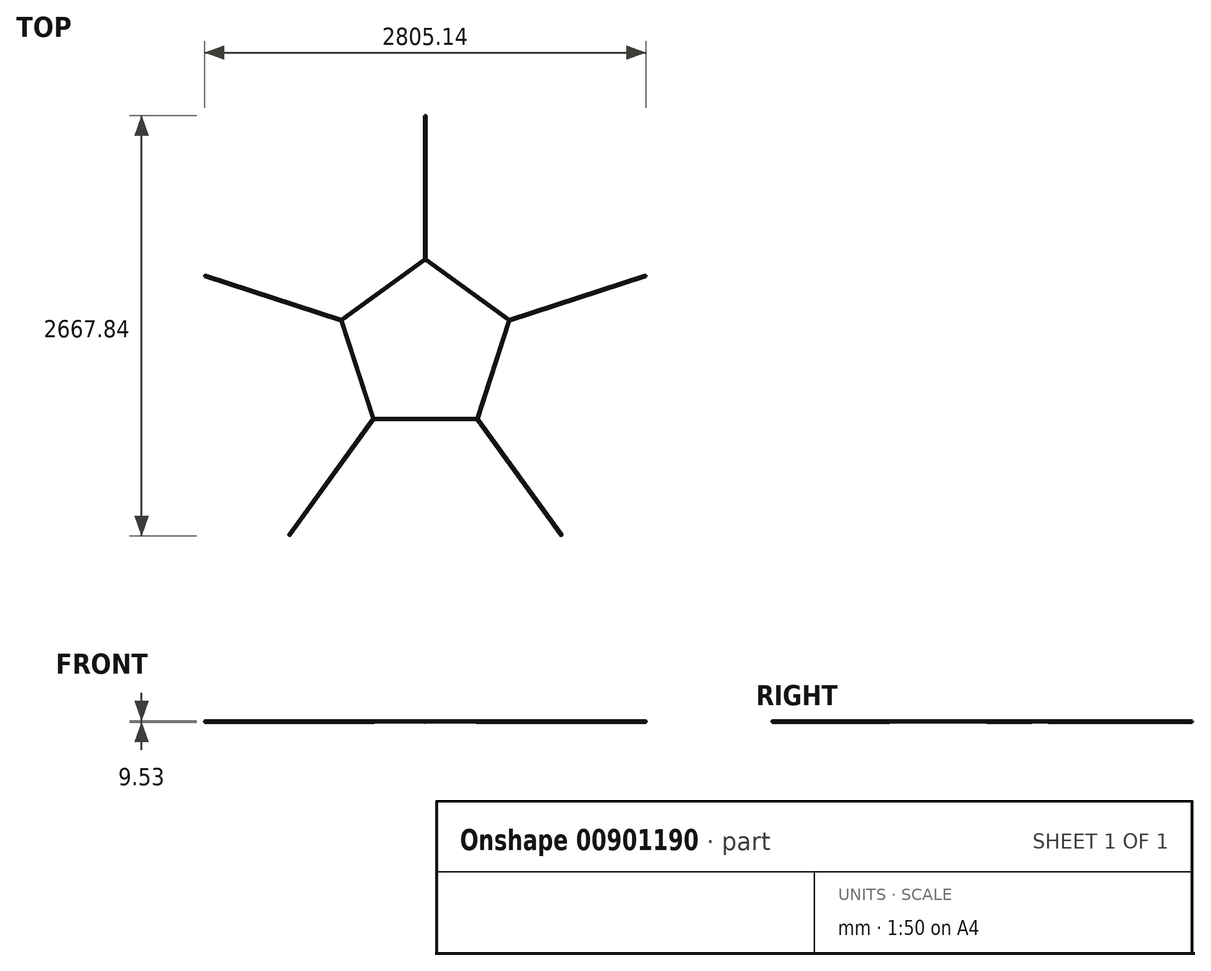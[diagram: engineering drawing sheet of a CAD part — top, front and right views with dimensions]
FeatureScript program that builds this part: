
annotation { "Feature Type Name" : "Feature", "Feature Type Description" : "" }
export const myFeature = defineFeature(function(context is Context, id is Id, definition is map)
    precondition{}
    {
        {
            var Q0;
            Q0=qCreatedBy(makeId("Top.planeOp"),FACE);
            var sketch = newSketch(context, id + "F0", { "sketchPlane" : qUnion([Q0])});
            skCircle(sketch, "E0.cCircle", {"center": v(0, 0) * mm, "radius": 450.85 * mm, "construction": true});
            skLineSegment(sketch, "E0.0", {"start": v(0, 557.28) * mm, "end": v(530, 172.2) * mm});
            skLineSegment(sketch, "E0.1", {"start": v(530, 172.2) * mm, "end": v(327.56, -450.85) * mm});
            skLineSegment(sketch, "E0.2", {"start": v(327.56, -450.85) * mm, "end": v(-327.56, -450.85) * mm});
            skLineSegment(sketch, "E0.3", {"start": v(-327.56, -450.85) * mm, "end": v(-530, 172.2) * mm});
            skLineSegment(sketch, "E0.4", {"start": v(-530, 172.2) * mm, "end": v(0, 557.28) * mm});
            skPoint(sketch, "E0.0.midPoint", {"position": v(265, 364.75) * mm});
            skCircle(sketch, "E1.cCircle", {"center": v(0, 0) * mm, "radius": 457.2 * mm, "construction": true});
            skLineSegment(sketch, "E1.0", {"start": v(0, 565.13) * mm, "end": v(537.47, 174.63) * mm});
            skLineSegment(sketch, "E1.1", {"start": v(537.47, 174.63) * mm, "end": v(332.18, -457.2) * mm});
            skLineSegment(sketch, "E1.2", {"start": v(332.18, -457.2) * mm, "end": v(-332.18, -457.2) * mm});
            skLineSegment(sketch, "E1.3", {"start": v(-332.18, -457.2) * mm, "end": v(-537.47, 174.63) * mm});
            skLineSegment(sketch, "E1.4", {"start": v(-537.47, 174.63) * mm, "end": v(0, 565.13) * mm});
            skPoint(sketch, "E1.0.midPoint", {"position": v(268.74, 369.88) * mm});
            skLineSegment(sketch, "E2", {"start": v(0, 0) * mm, "end": v(0, 903.65) * mm, "construction": true});
            skSolve(sketch);
        }
        {
            var Q0;
            Q0=makeQuery(id+"F0.imprint","IMPRINT",FACE,{"disambiguationData":[TD([[makeQuery(id+"F0.imprint","IMPRINT",EDGE,{"derivedFrom":sQuery(id+"F0.wireOp",EDGE,"E0.0")}),1.0]])]});
            extrude(context, id + "F1", {"entities" : qUnion([Q0]), "depth" : 6.35 * mm, "offsetDistance" : 25.4 * mm});
        }
        {
            var Q0;
            Q0=qCreatedBy(makeId("Front.planeOp"),FACE);
            var sketch = newSketch(context, id + "F2", { "sketchPlane" : qUnion([Q0])});
            skCircle(sketch, "E3", {"center": v(0, 3.18) * mm, "radius": 4.76 * mm});
            skSolve(sketch);
        }
        {
            var Q0;
            Q0=qCreatedBy(makeId("Front.planeOp"),FACE);
            var sketch = newSketch(context, id + "F3", { "sketchPlane" : qUnion([Q0])});
            skLineSegment(sketch, "E4", {"start": v(0, 0) * mm, "end": v(0, 50.6) * mm});
            skSolve(sketch);
        }
        {
            var Q0;
            Q0=makeQuery(id+"F2.imprint","IMPRINT",FACE,{"disambiguationData":[TD([[makeQuery(id+"F2.imprint","IMPRINT",EDGE,{"derivedFrom":sQuery(id+"F2.wireOp",EDGE,"E3")}),1.0]])]});
            extrude(context, id + "F4", {"entities" : qUnion([Q0]), "operationType" : NewBodyOperationType.ADD, "oppositeDirection" : true, "depth" : 1473.2 * mm, "offsetDistance" : 25.4 * mm});
        }
        {
            var Q0;
            Q0=makeQuery(id+"F1.opExtrude","SWEPT_BODY",BODY,{"disambiguationData":[OSD([sQuery(id+"F0.wireOp",EDGE,"E0.0"),sQuery(id+"F0.wireOp",EDGE,"E0.1"),sQuery(id+"F0.wireOp",EDGE,"E0.2"),sQuery(id+"F0.wireOp",EDGE,"E0.3"),sQuery(id+"F0.wireOp",EDGE,"E0.4"),sQuery(id+"F0.wireOp",EDGE,"E1.0"),sQuery(id+"F0.wireOp",EDGE,"E1.1"),sQuery(id+"F0.wireOp",EDGE,"E1.2"),sQuery(id+"F0.wireOp",EDGE,"E1.3"),sQuery(id+"F0.wireOp",EDGE,"E1.4")])]});
            var Q1;
            Q1=sQuery(id+"F3.wireOp",EDGE,"E4");
            circularPattern(context, id + "F5", {"operationType" : NewBodyOperationType.ADD, "entities" : qUnion([Q0]), "axis" : qUnion([Q1]), "angle" : 360 * degree, "instanceCount" : 5, "equalSpace" : true});
        }
        {
            var Q0;
            Q0=qCreatedBy(makeId("Top.planeOp"),FACE);
            var sketch = newSketch(context, id + "F6", { "sketchPlane" : qUnion([Q0])});
            skCircle(sketch, "E5.cCircle", {"center": v(0, 0) * mm, "radius": 450.85 * mm, "construction": true});
            skLineSegment(sketch, "E5.0", {"start": v(-530, 172.2) * mm, "end": v(0, 557.28) * mm});
            skLineSegment(sketch, "E5.1", {"start": v(0, 557.28) * mm, "end": v(530, 172.2) * mm});
            skLineSegment(sketch, "E5.2", {"start": v(530, 172.2) * mm, "end": v(327.56, -450.85) * mm});
            skLineSegment(sketch, "E5.3", {"start": v(327.56, -450.85) * mm, "end": v(-327.56, -450.85) * mm});
            skLineSegment(sketch, "E5.4", {"start": v(-327.56, -450.85) * mm, "end": v(-530, 172.2) * mm});
            skPoint(sketch, "E5.0.midPoint", {"position": v(-265, 364.75) * mm});
            skLineSegment(sketch, "E6", {"start": v(0, 0) * mm, "end": v(0, 1602.82) * mm, "construction": true});
            skSolve(sketch);
        }
        {
            var Q0;
            Q0=makeQuery(id+"F6.imprint","IMPRINT",FACE,{"disambiguationData":[TD([[makeQuery(id+"F6.imprint","IMPRINT",EDGE,{"derivedFrom":sQuery(id+"F6.wireOp",EDGE,"E5.0")}),-1.0]])]});
            extrude(context, id + "F7", {"entities" : qUnion([Q0]), "operationType" : NewBodyOperationType.REMOVE, "oppositeDirection" : true, "depth" : 25.4 * mm, "offsetDistance" : 25.4 * mm, "hasSecondDirection" : true, "secondDirectionOppositeDirection" : false, "secondDirectionDepth" : 25.4 * mm});
        }
    });
